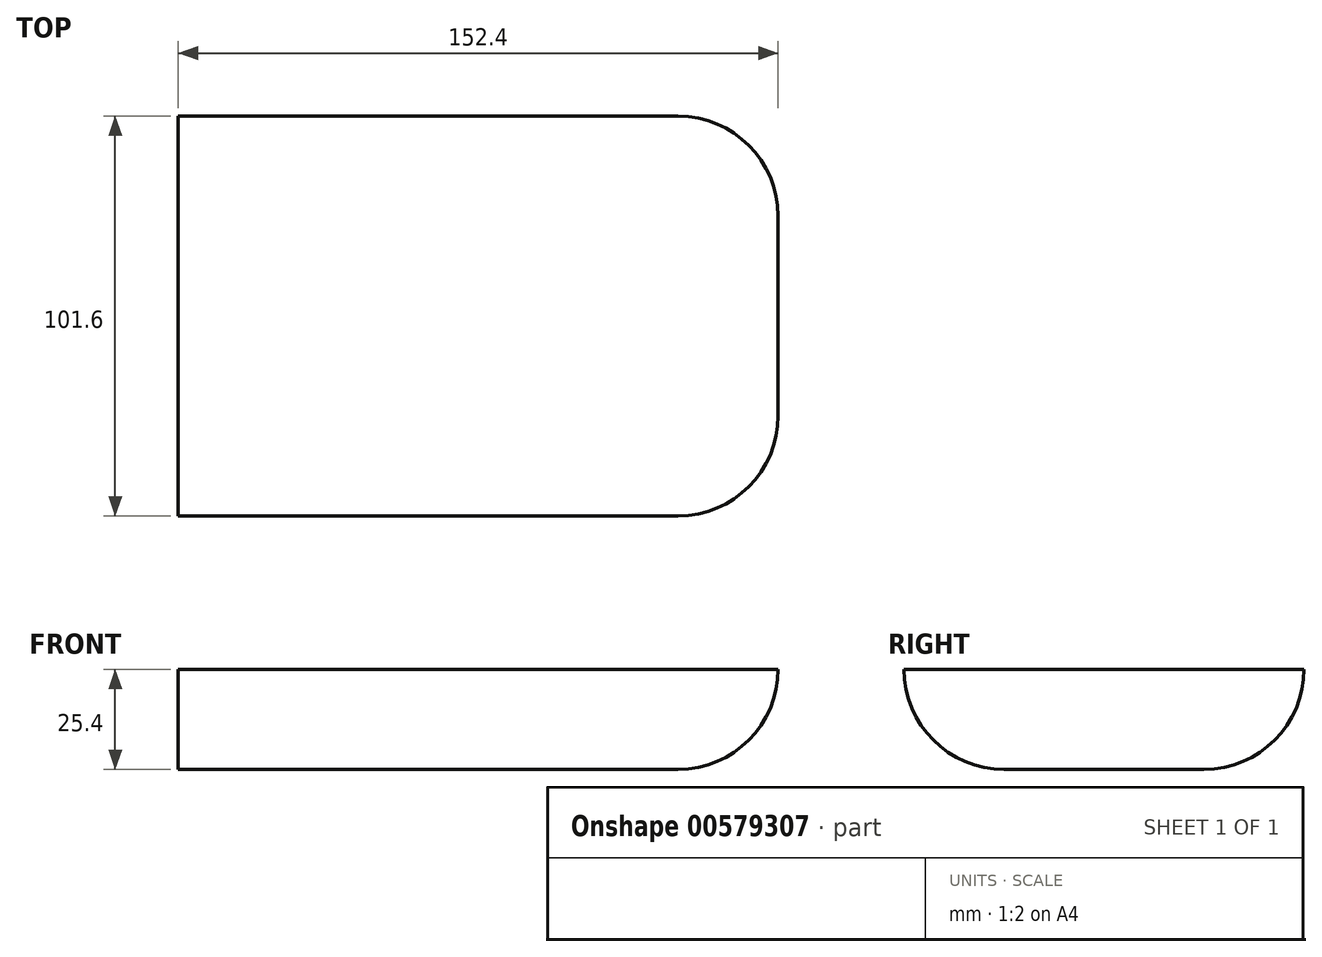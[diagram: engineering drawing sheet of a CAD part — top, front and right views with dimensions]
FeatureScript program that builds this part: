
annotation { "Feature Type Name" : "Feature", "Feature Type Description" : "" }
export const myFeature = defineFeature(function(context is Context, id is Id, definition is map)
    precondition{}
    {
        {
            var Q0;
            Q0=qCreatedBy(makeId("Front.planeOp"),FACE);
            var sketch = newSketch(context, id + "F0", { "sketchPlane" : qUnion([Q0])});
            skLineSegment(sketch, "E0.bottom", {"start": v(-90.5, 22.37) * mm, "end": v(36.5, 22.37) * mm});
            skLineSegment(sketch, "E0.top", {"start": v(-90.5, -3.03) * mm, "end": v(36.5, -3.03) * mm});
            skLineSegment(sketch, "E0.left", {"start": v(-90.5, 22.37) * mm, "end": v(-90.5, -3.03) * mm});
            skLineSegment(sketch, "E0.right", {"start": v(36.5, 22.37) * mm, "end": v(36.5, -3.03) * mm});
            skLineSegment(sketch, "E1", {"start": v(36.5, 22.37) * mm, "end": v(61.9, 22.37) * mm});
            skArc(sketch, "E2", {"start": v(36.5, -3.03) * mm, "mid": v(54.46, 4.41) * mm, "end": v(61.9, 22.37) * mm});
            skSolve(sketch);
        }
        {
            var Q0;
            Q0 = qSketchRegion(id + "F0", true);
            extrude(context, id + "F1", {"entities" : qUnion([Q0]), "depth" : 25.4 * mm, "offsetDistance" : 25.4 * mm});
        }
        {
            var Q0;
            Q0=makeQuery(id+"F1.opExtrude","CAP_FACE",FACE,{"disambiguationData":[OSD([sQuery(id+"F0.wireOp",EDGE,"E0.bottom"),sQuery(id+"F0.wireOp",EDGE,"E0.top"),sQuery(id+"F0.wireOp",EDGE,"E0.left"),sQuery(id+"F0.wireOp",EDGE,"E1"),sQuery(id+"F0.wireOp",EDGE,"E2")])],"isStart":false});
            extrude(context, id + "F2", {"entities" : qUnion([Q0]), "operationType" : NewBodyOperationType.ADD, "depth" : 76.2 * mm, "offsetDistance" : 25.4 * mm});
        }
        {
            var Q0;
            Q0=makeQuery(id+"F2.opExtrude","CAP_EDGE",EDGE,{"disambiguationData":[OSD([sQuery(id+"F0.wireOp",EDGE,"E0.top")])],"isStart":false});
            fillet(context, id + "F3", {"entities" : qUnion([Q0]), "radius" : 25.4 * mm, "tangentPropagation" : true, "allowEdgeOverflow" : false});
        }
        {
            var Q0;
            Q0=makeQuery(id+"F1.opExtrude","CAP_EDGE",EDGE,{"disambiguationData":[OSD([sQuery(id+"F0.wireOp",EDGE,"E0.top")])],"isStart":true});
            fillet(context, id + "F4", {"entities" : qUnion([Q0]), "radius" : 25.4 * mm, "tangentPropagation" : true, "allowEdgeOverflow" : false});
        }
    });
